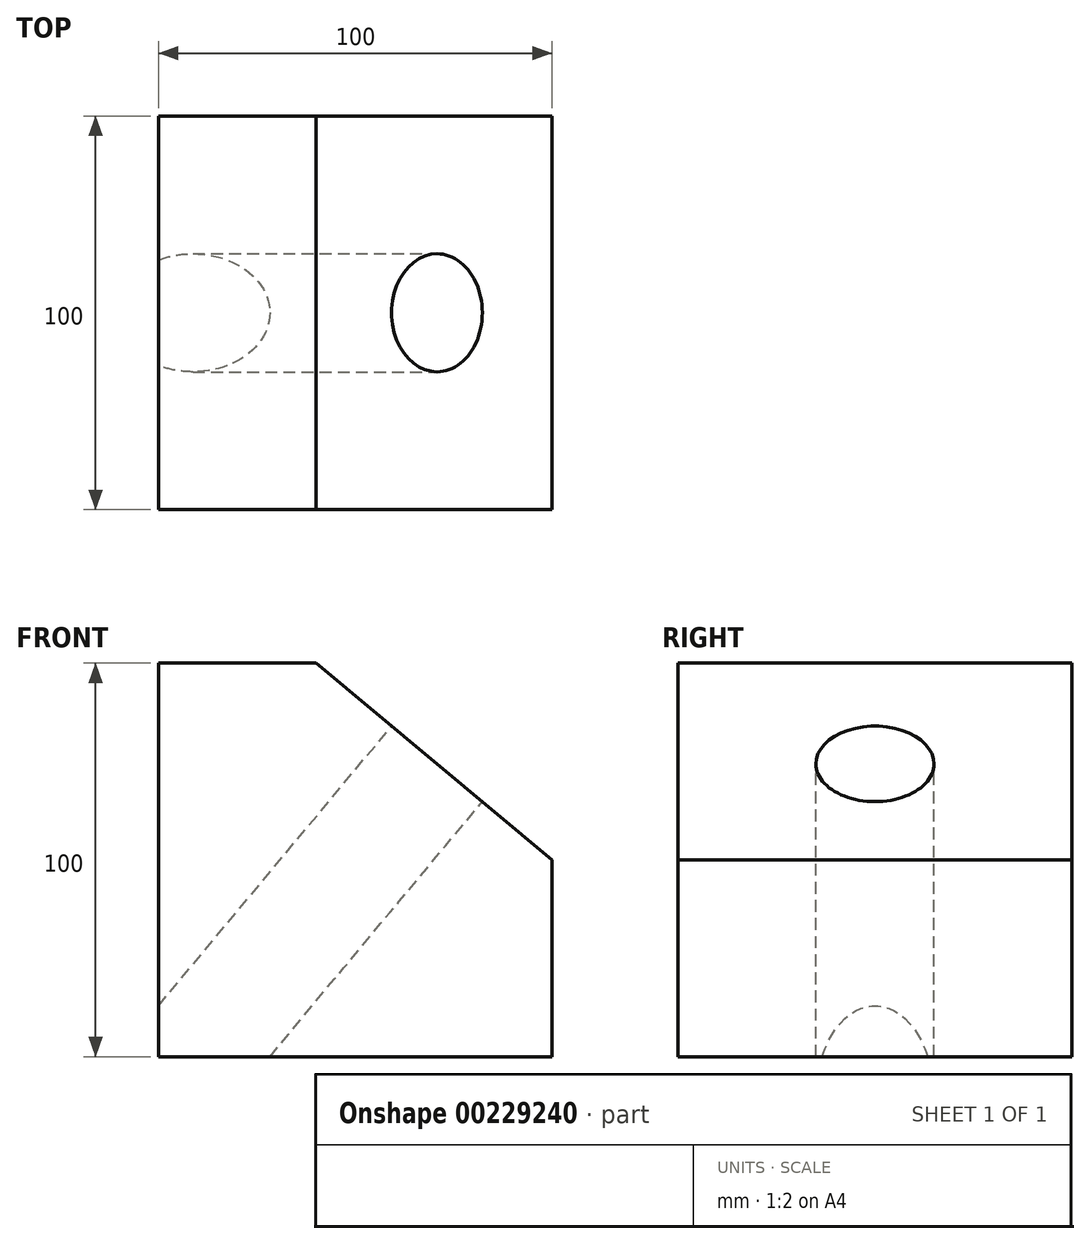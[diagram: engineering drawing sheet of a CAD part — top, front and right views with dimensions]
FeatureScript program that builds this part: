
annotation { "Feature Type Name" : "Feature", "Feature Type Description" : "" }
export const myFeature = defineFeature(function(context is Context, id is Id, definition is map)
    precondition{}
    {
        {
            var Q0;
            Q0=qCreatedBy(makeId("Front.planeOp"),FACE);
            var sketch = newSketch(context, id + "F0", { "sketchPlane" : qUnion([Q0])});
            skLineSegment(sketch, "E0.bottom", {"start": v(0, 100) * mm, "end": v(100, 100) * mm});
            skLineSegment(sketch, "E0.top", {"start": v(0, 0) * mm, "end": v(100, 0) * mm});
            skLineSegment(sketch, "E0.left", {"start": v(0, 100) * mm, "end": v(0, 0) * mm});
            skLineSegment(sketch, "E0.right", {"start": v(100, 100) * mm, "end": v(100, 0) * mm});
            skSolve(sketch);
        }
        {
            var Q0;
            Q0 = qSketchRegion(id + "F0", true);
            extrude(context, id + "F1", {"entities" : qUnion([Q0]), "oppositeDirection" : true, "depth" : 100 * mm});
        }
        {
            var Q0;
            Q0=makeQuery(id+"F1.opExtrude","CAP_FACE",FACE,{"disambiguationData":[OSD([sQuery(id+"F0.wireOp",EDGE,"E0.bottom"),sQuery(id+"F0.wireOp",EDGE,"E0.top"),sQuery(id+"F0.wireOp",EDGE,"E0.left"),sQuery(id+"F0.wireOp",EDGE,"E0.right")])],"isStart":true});
            var sketch = newSketch(context, id + "F2", { "sketchPlane" : qUnion([Q0])});
            skLineSegment(sketch, "E1", {"start": v(40, 100) * mm, "end": v(100, 50) * mm});
            skLineSegment(sketch, "E2", {"start": v(100, 50) * mm, "end": v(110, 50) * mm});
            skLineSegment(sketch, "E3", {"start": v(40, 100) * mm, "end": v(40, 110) * mm});
            skLineSegment(sketch, "E4", {"start": v(40, 110) * mm, "end": v(110, 110) * mm});
            skLineSegment(sketch, "E5", {"start": v(110, 110) * mm, "end": v(110, 50) * mm});
            skSolve(sketch);
        }
        {
            var Q0;
            Q0 = qSketchRegion(id + "F2", true);
            extrude(context, id + "F3", {"entities" : qUnion([Q0]), "operationType" : NewBodyOperationType.REMOVE, "endBound" : BoundingType.THROUGH_ALL, "oppositeDirection" : true, "depth" : 51.18 * mm});
        }
        {
            var Q0;
            Q0=makeQuery(id+"F3.boolean.opBoolean","COPY",FACE,{"derivedFrom":makeQuery(id+"F3.opExtrude","SWEPT_FACE",FACE,{"disambiguationData":[OSD([sQuery(id+"F2.wireOp",EDGE,"E1")])]})});
            var sketch = newSketch(context, id + "F4", { "sketchPlane" : qUnion([Q0])});
            skCircle(sketch, "E6", {"center": v(6.71, 50) * mm, "radius": 15 * mm});
            skSolve(sketch);
        }
        {
            var Q0;
            Q0 = qSketchRegion(id + "F4", true);
            extrude(context, id + "F5", {"entities" : qUnion([Q0]), "operationType" : NewBodyOperationType.REMOVE, "endBound" : BoundingType.THROUGH_ALL, "oppositeDirection" : true, "depth" : 37.34 * mm});
        }
    });
